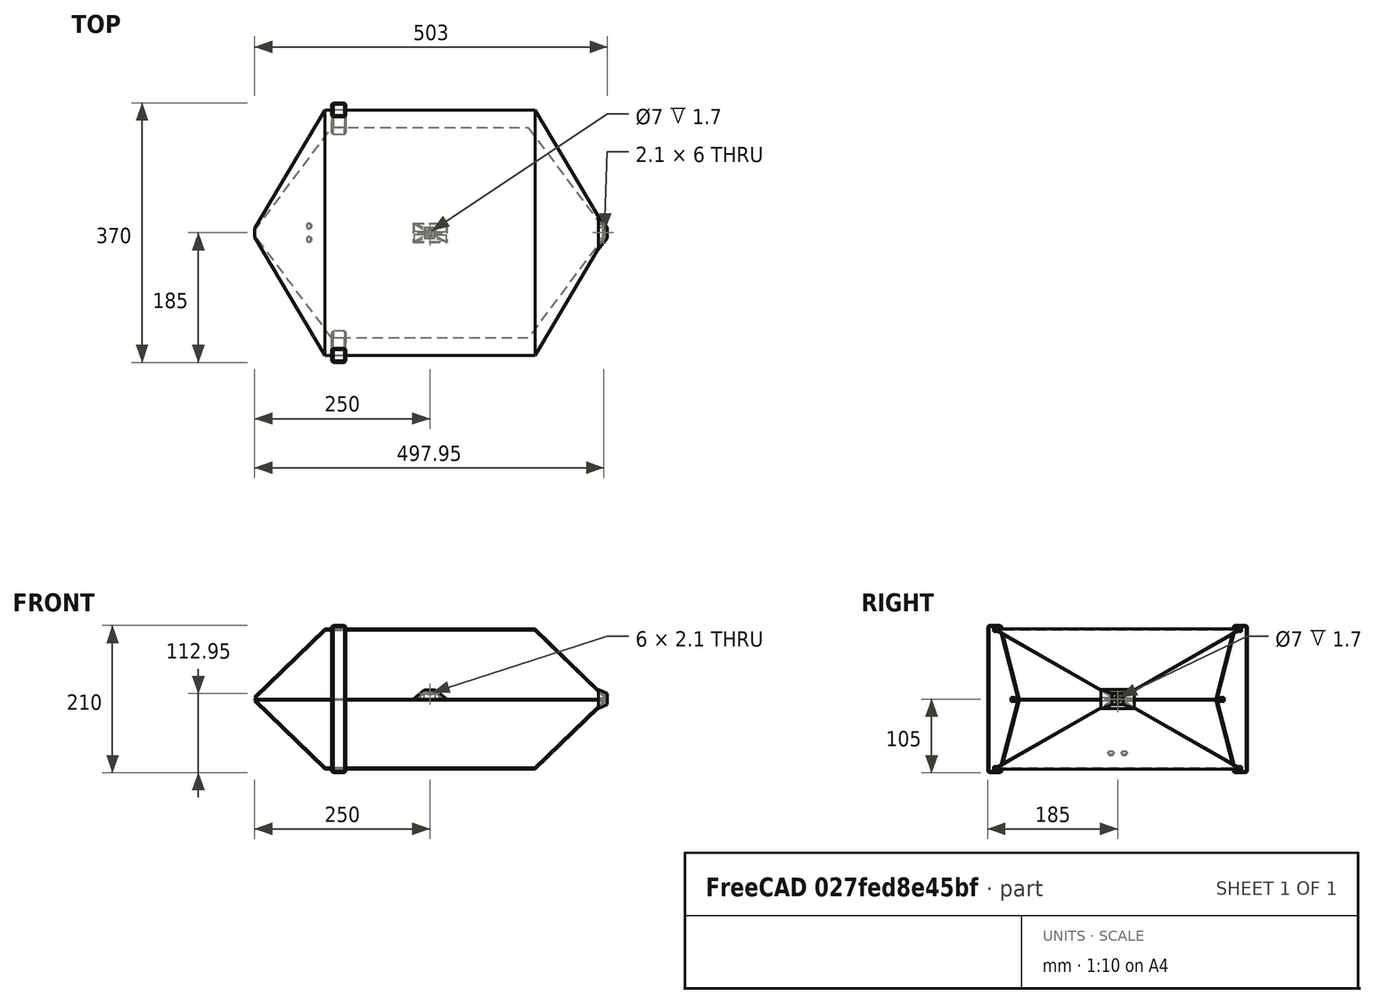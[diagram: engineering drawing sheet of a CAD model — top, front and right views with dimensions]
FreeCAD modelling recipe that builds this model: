
FCSTD DOCUMENT  (FreeCAD 0.21R33694 (Git))
Label: OpenTEMCell
License: All rights reserved
LicenseURL: http://en.wikipedia.org/wiki/All_rights_reserved
objects: TechDraw::DrawViewDimension×23, Sketcher::SketchObject×8, PartDesign::Pad×6, PartDesign::Body×5, PartDesign::AdditiveWedge×5, PartDesign::Mirrored×4, Part::Mirroring×4, App::Part×3, TechDraw::DrawViewPart×3, PartDesign::SubtractiveWedge×3, PartDesign::CoordinateSystem×2, TechDraw::DrawSVGTemplate×2, TechDraw::DrawViewBalloon×2, TechDraw::DrawPage×2, Spreadsheet::Sheet×1, PartDesign::Pocket×1, PartDesign::Chamfer×1, TechDraw::DrawViewSpreadsheet×1, TechDraw::DrawViewAnnotation×1, PartDesign::SubtractiveCylinder×1
note: 73 computed .brp shape members not serialized (recipe doc carries the construction recipe); baked Part::Feature solids carry a one-line shape summary decoded from their .brp

FEATURE [Spreadsheet::Sheet] Spreadsheet  label="Params"
  cells = A1='ShieldWidth; B1(ShieldWidth)==350 mm; D1='Width of the outer shield sections (affects FringeCapacitance); A2='SeptumWidth; B2(SeptumWidth)==300 mm; D2='Width of the middle septum layer (affects ApproxImpedance); A3='CenterSectionLength; B3(CenterSectionLength)==300 mm; D3='Length of the square center section of shields; A4='SeptumCenterSectionLength; B4(SeptumCenterSectionLength)==280 mm; D4='Length of the square center section of septum; A5='TaperSectionLength; B5(TaperSectionLength)==100 mm; D5='Tapered section horizontal length of shields; A7='UpperHeight; B7(UpperHeight)==100 mm; D7='Distance between septum and upper shield; A8='LowerHeight; B8(LowerHeight)==100 mm; D8='Distance between septum and lower shield; A10='ShieldTaperEndWidth; B10(ShieldTaperEndWidth)==12 mm; D10='For mounting the coaxial connectors; A11='ShieldTaperEndHeight; B11(ShieldTaperEndHeight)==6 mm; A12='SeptumTaperEndWidth; B12(SeptumTaperEndWidth)==6 mm; A13='MaterialThickness; B13(MaterialThickness)==1.6 mm; A15='Parameters below are calculated from inputs above; A17='SeptumTotalLength; B17(SeptumTotalLength)==CenterSectionLength + 2 * TaperSectionLength; D17='Total length for the middle septum layer; A18='UpperShieldTaperMaterialLength; B18(UpperShieldTaperMaterialLength)==sqrt((UpperHeight - ShieldTaperEndHeight / 2) ^ 2 + TaperSectionLength ^ 2); D18='Material length at the taper slope on each end of upper shield; A19='LowerShieldTaperMaterialLength; B19(LowerShieldTaperMaterialLength)==sqrt((LowerHeight - ShieldTaperEndHeight / 2) ^ 2 + TaperSectionLength ^ 2); A20='UpperShieldTotalLength; B20(UpperShieldTotalLength)==CenterSectionLength + UpperShieldTaperMaterialLength * 2; D20='Total material length for upper shield; A21='LowerShieldTotalLength; B21(LowerShieldTotalLength)==CenterSectionLength + LowerShieldTaperMaterialLength * 2; A23='FringeCapacitance; B23(FringeCapacitance)=0.03; C23='(empirical); A24='ApproxImpedance; B24==94 / (SeptumWidth / (UpperHeight + LowerHeight) + FringeCapacitance / 0.0885); C24='(ohm); D24='(valid only for UpperHeight = LowerHeight); A26='UpperTaperAngle; B26(UpperTaperAngle)==atan((UpperHeight - ShieldTaperEndHeight / 2) / TaperSectionLength); A27='LowerTaperAngle; B27(LowerTaperAngle)==atan((LowerHeight - ShieldTaperEndHeight / 2) / TaperSectionLength)
FEATURE [Sketcher::SketchObject] Sketch  label="SeptumSketch"
  FullyConstrained = true
  MapMode = 5
  Support = -> [XY_Plane001]
  expr: Constraints[14] = <<Params>>.SeptumTotalLength
  expr: Constraints[15] = <<Params>>.SeptumCenterSectionLength
  expr: Constraints[16] = <<Params>>.SeptumWidth
  expr: Constraints[17] = <<Params>>.SeptumTaperEndWidth
  sketch-geometry (8):
    g0: LineSegment StartX=-250 StartY=-3 StartZ=0 EndX=-250 EndY=3 EndZ=0
    g1: LineSegment StartX=-250 StartY=3 StartZ=0 EndX=-140 EndY=150 EndZ=0
    g2: LineSegment StartX=-140 StartY=150 StartZ=0 EndX=140 EndY=150 EndZ=0
    g3: LineSegment StartX=140 StartY=150 StartZ=0 EndX=250 EndY=3 EndZ=0
    g4: LineSegment StartX=250 StartY=3 StartZ=0 EndX=250 EndY=-3 EndZ=0
    g5: LineSegment StartX=250 StartY=-3 StartZ=0 EndX=140 EndY=-150 EndZ=0
    g6: LineSegment StartX=140 StartY=-150 StartZ=0 EndX=-140 EndY=-150 EndZ=0
    g7: LineSegment StartX=-140 StartY=-150 StartZ=0 EndX=-250 EndY=-3 EndZ=0
  constraints (18):
    c: Coincident(g0,g1)
    c: Coincident(g1,g2)
    c: Coincident(g3,g4)
    c: Coincident(g4,g5)
    c: Coincident(g5,g6)
    c: Coincident(g6,g7)
    c: Coincident(g7,g0)
    c: Symmetric(g6,g1,g-1)
    c: Symmetric(g5,g2,g-1)
    c: Symmetric(g2,g1,g-2)
    c: Coincident(g3,g2)
    c: Symmetric(g3,g4,g-1)
    c: Symmetric(g4,g0,g-2)
    c: Symmetric(g0,g3,g-2)
    c: DistanceX(g0,g4) = 500
    c: DistanceX(g2,g2) = 280
    c: DistanceY(g6,g1) = 300
    c: DistanceY(g0,g0) = 6
FEATURE [PartDesign::Pad] Pad  label="Septum001"
  Direction = (0,0,1)
  Length = 1.6
  Length2 = 10
  Profile = -> Sketch
  ReferenceAxis = -> Sketch [N_Axis]
  Reversed = true
  Type = 0
  expr: Length = <<Params>>.MaterialThickness
FEATURE [PartDesign::Body] Body  label="Septum"
  Group = -> [Sketch,Pad]
  Origin = -> Origin001
  Tip = -> Pad
FEATURE [Sketcher::SketchObject] Sketch001  label="UpperShieldCenterSectionSketch"
  FullyConstrained = true
  MapMode = 5
  Support = -> [XY_Plane]
  expr: Constraints[8] = <<Params>>.CenterSectionLength
  expr: Constraints[9] = <<Params>>.ShieldWidth
  sketch-geometry (4):
    g0: LineSegment StartX=-150 StartY=175 StartZ=0 EndX=150 EndY=175 EndZ=0
    g1: LineSegment StartX=150 StartY=175 StartZ=0 EndX=150 EndY=-175 EndZ=0
    g2: LineSegment StartX=150 StartY=-175 StartZ=0 EndX=-150 EndY=-175 EndZ=0
    g3: LineSegment StartX=-150 StartY=-175 StartZ=0 EndX=-150 EndY=175 EndZ=0
  constraints (11):
    c: Coincident(g0,g1)
    c: Coincident(g1,g2)
    c: Coincident(g2,g3)
    c: Coincident(g3,g0)
    c: Horizontal(g0)
    c: Horizontal(g2)
    c: Vertical(g1)
    c: Vertical(g3)
    c: DistanceX(g0,g0) = 300
    c: DistanceY(g3,g3) = 350
    c: Symmetric(g0,g2,g-1)
FEATURE [PartDesign::Pad] Pad001  label="UpperShieldCenterSection"
  Direction = (0,0,1)
  Length = 1.6
  Length2 = 10
  Profile = -> Sketch001
  ReferenceAxis = -> Sketch001 [N_Axis]
  Type = 0
  expr: Length = <<Params>>.MaterialThickness
FEATURE [PartDesign::CoordinateSystem] Local_CS  label="TaperCoordinateSystem"
  AttacherType = Attacher::AttachEngine3D
  AttachmentOffset = pos=(-150,0,0) rot=(0,1,0;0.770171rad)
  MapMode = 5
  Placement = pos=(-150,0,0) rot=(0,1,0;0.770171rad)
  Support = -> [XY_Plane]
  expr: .AttachmentOffset.Base.x = -<<Params>>.CenterSectionLength / 2
  expr: .AttachmentOffset.Rotation.Pitch = <<Params>>.UpperTaperAngle
  expr: .AttachmentOffset.Rotation.Roll = 0
FEATURE [Sketcher::SketchObject] Sketch002  label="UpperShieldTaperSectionSketch"
  FullyConstrained = true
  MapMode = 5
  Placement = pos=(-150,0,0) rot=(0,1,0;0.770171rad)
  Support = -> [Local_CS]
  expr: .AttachmentOffset.Rotation.Angle = 0
  expr: Constraints[6] = <<Params>>.ShieldTaperEndWidth
  expr: Constraints[7] = <<Params>>.ShieldWidth
  expr: Constraints[8] = <<Params>>.UpperShieldTaperMaterialLength
  sketch-geometry (4):
    g0: LineSegment StartX=1e-16 StartY=-175 StartZ=0 EndX=0 EndY=175 EndZ=0
    g1: LineSegment StartX=0 StartY=175 StartZ=0 EndX=-139.316 EndY=6 EndZ=0
    g2: LineSegment StartX=-139.316 StartY=6 StartZ=0 EndX=-139.316 EndY=-6 EndZ=0
    g3: LineSegment StartX=-139.316 StartY=-6 StartZ=0 EndX=0 EndY=-175 EndZ=0
  constraints (10):
    c: Coincident(g0,g1)
    c: Coincident(g1,g2)
    c: Coincident(g2,g3)
    c: Coincident(g3,g0)
    c: Symmetric(g0,g0,g-1)
    c: Symmetric(g1,g2,g-1)
    c: DistanceY(g2,g2) = 12
    c: DistanceY(g0,g0) = 350
    c: DistanceX(g1,g0) = 139.316
    c: PointOnObject(g0,g-2)
FEATURE [PartDesign::Pad] Pad002  label="UpperShieldTaperSection"
  BaseFeature = -> Pad001
  Direction = (0.696258,0,0.717792)
  Length = 1.6
  Length2 = 10
  Profile = -> Sketch002
  ReferenceAxis = -> Sketch002 [N_Axis]
  Type = 0
  expr: Length = <<Params>>.MaterialThickness
FEATURE [PartDesign::Mirrored] Mirrored  label="UpperTaperMirror"
  BaseFeature = -> Pad002
  MirrorPlane = -> YZ_Plane
  Originals = -> [Pad002]
FEATURE [PartDesign::Body] Body001  label="UpperShield"
  Group = -> [Sketch001,Pad001,Sketch002,Local_CS,Pad002,Mirrored]
  Origin = -> Origin
  Placement = pos=(0,0,100) rot=(1,0,0;3.14159rad)
  Tip = -> Mirrored
  expr: .Placement.Base.z = <<Params>>.UpperHeight
FEATURE [PartDesign::CoordinateSystem] Local_CS001  label="TaperCoordinateSystem001"
  AttacherType = Attacher::AttachEngine3D
  AttachmentOffset = pos=(-150,0,0) rot=(0,1,0;0.770171rad)
  MapMode = 5
  Placement = pos=(-150,0,0) rot=(0,1,0;0.770171rad)
  Support = -> [XY_Plane002]
  expr: .AttachmentOffset.Base.x = -<<Params>>.CenterSectionLength / 2
  expr: .AttachmentOffset.Rotation.Pitch = <<Params>>.LowerTaperAngle
  expr: .AttachmentOffset.Rotation.Roll = 0
FEATURE [Sketcher::SketchObject] Sketch003  label="LowerShieldCenterSectionSketch"
  FullyConstrained = true
  MapMode = 5
  Support = -> [XY_Plane002]
  expr: Constraints[8] = <<Params>>.CenterSectionLength
  expr: Constraints[9] = <<Params>>.ShieldWidth
  sketch-geometry (4):
    g0: LineSegment StartX=-150 StartY=175 StartZ=0 EndX=150 EndY=175 EndZ=0
    g1: LineSegment StartX=150 StartY=175 StartZ=0 EndX=150 EndY=-175 EndZ=0
    g2: LineSegment StartX=150 StartY=-175 StartZ=0 EndX=-150 EndY=-175 EndZ=0
    g3: LineSegment StartX=-150 StartY=-175 StartZ=0 EndX=-150 EndY=175 EndZ=0
  constraints (11):
    c: Coincident(g0,g1)
    c: Coincident(g1,g2)
    c: Coincident(g2,g3)
    c: Coincident(g3,g0)
    c: Horizontal(g0)
    c: Horizontal(g2)
    c: Vertical(g1)
    c: Vertical(g3)
    c: DistanceX(g0,g0) = 300
    c: DistanceY(g3,g3) = 350
    c: Symmetric(g0,g2,g-1)
FEATURE [PartDesign::Pad] Pad003  label="LowerShieldCenterSection"
  Direction = (0,0,1)
  Length = 1.6
  Length2 = 10
  Profile = -> Sketch003
  ReferenceAxis = -> Sketch003 [N_Axis]
  Type = 0
  expr: Length = <<Params>>.MaterialThickness
FEATURE [Sketcher::SketchObject] Sketch004  label="LowerShieldTaperSectionSketch"
  FullyConstrained = true
  MapMode = 5
  Placement = pos=(-150,0,0) rot=(0,1,0;0.770171rad)
  Support = -> [Local_CS001]
  expr: .AttachmentOffset.Rotation.Angle = 0
  expr: Constraints[6] = <<Params>>.ShieldTaperEndWidth
  expr: Constraints[7] = <<Params>>.ShieldWidth
  expr: Constraints[8] = <<Params>>.LowerShieldTaperMaterialLength
  sketch-geometry (4):
    g0: LineSegment StartX=0 StartY=-175 StartZ=0 EndX=0 EndY=175 EndZ=0
    g1: LineSegment StartX=0 StartY=175 StartZ=0 EndX=-139.316 EndY=6 EndZ=0
    g2: LineSegment StartX=-139.316 StartY=6 StartZ=0 EndX=-139.316 EndY=-6 EndZ=0
    g3: LineSegment StartX=-139.316 StartY=-6 StartZ=0 EndX=0 EndY=-175 EndZ=0
  constraints (10):
    c: Coincident(g0,g1)
    c: Coincident(g1,g2)
    c: Coincident(g2,g3)
    c: Coincident(g3,g0)
    c: Symmetric(g0,g0,g-1)
    c: Symmetric(g1,g2,g-1)
    c: DistanceY(g2,g2) = 12
    c: DistanceY(g0,g0) = 350
    c: DistanceX(g1,g0) = 139.316
    c: PointOnObject(g0,g-2)
FEATURE [PartDesign::Pad] Pad004  label="LowerShieldTaperSection"
  BaseFeature = -> Pad003
  Direction = (0.696258,0,0.717792)
  Length = 1.6
  Length2 = 10
  Profile = -> Sketch004
  ReferenceAxis = -> Sketch004 [N_Axis]
  Type = 0
  expr: Length = <<Params>>.MaterialThickness
FEATURE [PartDesign::Mirrored] Mirrored001  label="LowerTaperMirror"
  BaseFeature = -> Pad004
  MirrorPlane = -> YZ_Plane002
  Originals = -> [Pad004]
FEATURE [Sketcher::SketchObject] Sketch005  label="BindingPostHolesSketch"
  FullyConstrained = true
  MapMode = 5
  Placement = pos=(-150,0,0) rot=(0,1,0;0.770171rad)
  Support = -> [Local_CS001]
  sketch-geometry (2):
    g0: Circle CenterX=-32 CenterY=9.5 CenterZ=0 NormalX=0 NormalY=0 NormalZ=1 AngleXU=0 Radius=4
    g1: Circle CenterX=-32 CenterY=-9.5 CenterZ=0 NormalX=0 NormalY=0 NormalZ=1 AngleXU=0 Radius=4
  constraints (5):
    c: Symmetric(g0,g1,g-1)
    c: DistanceY(g1,g0) = 19
    c: Diameter(g0) = 8
    c: Equal(g1,g0)
    c: DistanceX(g1,g-1) = 32
FEATURE [PartDesign::Pocket] Pocket  label="BindingPostHoles"
  BaseFeature = -> Mirrored001
  Direction = (-0.696258,0,-0.717792)
  Length = 5
  Length2 = 5
  Profile = -> Sketch005
  ReferenceAxis = -> Sketch005 [N_Axis]
  Reversed = true
  Type = 1
FEATURE [PartDesign::Body] Body002  label="LowerShield"
  Group = -> [Sketch003,Pad003,Sketch004,Local_CS001,Pad004,Mirrored001,Sketch005,Pocket]
  Origin = -> Origin002
  Placement = pos=(0,0,-100) rot=(1,0,0;0rad)
  Tip = -> Pocket
  expr: .Placement.Base.z = -<<Params>>.LowerHeight
FEATURE [Sketcher::SketchObject] Sketch006  label="SideHolderSketch"
  FullyConstrained = true
  MapMode = 5
  Support = -> [XY_Plane003]
  expr: Constraints[31] = <<Params>>.LowerHeight
  expr: Constraints[38] = (<<Params>>.ShieldWidth - <<Params>>.SeptumWidth) / 2
  expr: Constraints[40] = <<Params>>.UpperHeight
  expr: Constraints[45] = <<Params>>.MaterialThickness + 5 mm
  expr: Constraints[46] = <<Params>>.MaterialThickness + 5 mm
  sketch-geometry (16):
    g0: LineSegment StartX=0 StartY=-105 StartZ=0 EndX=20 EndY=-105 EndZ=0
    g1: LineSegment StartX=20 StartY=-105 StartZ=0 EndX=20 EndY=-100 EndZ=0
    g2: LineSegment StartX=20 StartY=-100 StartZ=0 EndX=10 EndY=-100 EndZ=0
    g3: LineSegment StartX=10 StartY=-100 StartZ=0 EndX=10 EndY=-98.4 EndZ=0
    g4: LineSegment StartX=10 StartY=-98.4 StartZ=0 EndX=20 EndY=-98.4 EndZ=0
    g5: LineSegment StartX=20 StartY=-98.4 StartZ=0 EndX=45 EndY=-1.6 EndZ=0
    g6: LineSegment StartX=45 StartY=-1.6 StartZ=0 EndX=35 EndY=-1.6 EndZ=0
    g7: LineSegment StartX=35 StartY=-1.6 StartZ=0 EndX=35 EndY=0 EndZ=0
    g8: LineSegment StartX=35 StartY=0 StartZ=0 EndX=45 EndY=0 EndZ=0
    g9: LineSegment StartX=45 StartY=0 StartZ=0 EndX=20 EndY=98.4 EndZ=0
    g10: LineSegment StartX=20 StartY=98.4 StartZ=0 EndX=10 EndY=98.4 EndZ=0
    g11: LineSegment StartX=10 StartY=98.4 StartZ=0 EndX=10 EndY=100 EndZ=0
    g12: LineSegment StartX=10 StartY=100 StartZ=0 EndX=20 EndY=100 EndZ=0
    g13: LineSegment StartX=20 StartY=100 StartZ=0 EndX=20 EndY=105 EndZ=0
    g14: LineSegment StartX=20 StartY=105 StartZ=0 EndX=0 EndY=105 EndZ=0
    g15: LineSegment StartX=0 StartY=105 StartZ=0 EndX=0 EndY=-105 EndZ=0
  constraints (48):
    c: PointOnObject(g0,g-2)
    c: Horizontal(g0)
    c: Coincident(g0,g1)
    c: Vertical(g1)
    c: Coincident(g1,g2)
    c: Horizontal(g2)
    c: Coincident(g2,g3)
    c: Vertical(g3)
    c: Coincident(g3,g4)
    c: Horizontal(g4)
    c: Coincident(g4,g5)
    c: Coincident(g5,g6)
    c: Horizontal(g6)
    c: Coincident(g6,g7)
    c: Vertical(g7)
    c: Coincident(g7,g8)
    c: Horizontal(g8)
    c: Coincident(g8,g9)
    c: Coincident(g9,g10)
    c: Horizontal(g10)
    c: Coincident(g10,g11)
    c: Vertical(g11)
    c: Coincident(g11,g12)
    c: Horizontal(g12)
    c: Coincident(g12,g13)
    c: Vertical(g13)
    c: Coincident(g13,g14)
    c: PointOnObject(g14,g-2)
    c: Horizontal(g14)
    c: Coincident(g14,g15)
    c: Coincident(g15,g0)
    c: DistanceY(g2,g-1) = 100
    c: Vertical(g1,g4)
    c: Vertical(g9,g12)
    c: Vertical(g12,g1)
    c: Vertical(g8,g5)
    c: DistanceX(g0,g2) = 10
    c: Vertical(g3,g10)
    c: DistanceX(g3,g6) = 25
    c: DistanceX(g6,g6) = 10
    c: DistanceY(g-1,g11) = 100
    c: DistanceY(g13,g13) = 5
    c: DistanceY(g1,g1) = 5
    c: Equal(g4,g6)
    c: PointOnObject(g8,g-1)
    c: DistanceY(g10,g14) = 6.6
    c: DistanceY(g0,g3) = 6.6
    c: Equal(g3,g7)
FEATURE [PartDesign::Pad] Pad005  label="SideHolderBaseForm"
  Direction = (0,0,1)
  Length = 20
  Length2 = 10
  Profile = -> Sketch006
  ReferenceAxis = -> Sketch006 [N_Axis]
  Type = 0
FEATURE [PartDesign::Chamfer] Chamfer
  Angle = 45
  Base = -> Pad005 [Face18,Face17,Face16,Face15,Face1]
  BaseFeature = -> Pad005
  ChamferType = 0
  FlipDirection = false
  Size = 2
  Size2 = 1
  SupportTransform = false
  UseAllEdges = false
FEATURE [PartDesign::Body] Body003  label="SideHolder1"
  Group = -> [Sketch006,Pad005,Chamfer]
  Origin = -> Origin003
  Placement = pos=(120,-185,0) rot=(0.57735,0.57735,0.57735;2.0944rad)
  Tip = -> Chamfer
  expr: .Placement.Base.x = <<Params>>.SeptumCenterSectionLength / 2 - 20 mm
  expr: .Placement.Base.y = -<<Params>>.ShieldWidth / 2 - 10 mm
FEATURE [Part::Mirroring] mirror  label="SideHolder2 (mirror)"
  Base = (0,0,0)
  Normal = (1,0,0)
  Source = -> Body003
FEATURE [Part::Mirroring] mirror002  label="SideHolder4 (mirror)"
  Base = (0,0,0)
  Normal = (0,1,0)
  Source = -> Body003
FEATURE [Part::Mirroring] mirror003  label="SideHolder3 (mirror)"
  Base = (0,0,0)
  Normal = (1,0,0)
  Source = -> mirror002
FEATURE [App::Part] Part  label="SideHolders"
  Group = -> [Body003,mirror002,mirror003,mirror]
  Origin = -> Origin004
FEATURE [TechDraw::DrawSVGTemplate] Template
  Height = 297
  Orientation = 0
  Width = 210
FEATURE [TechDraw::DrawViewSpreadsheet] Sheet
  CellEnd = D27
  CellStart = A1
  Font = osifont
  LineWidth = 0.35
  LockPosition = false
  Rotation = 0
  Scale = 0.5
  ScaleType = 2
  Source = -> Spreadsheet
  Symbol = <blob: 18333 chars omitted>
  TextSize = 16
  X = 105.113
  Y = 218.016
FEATURE [TechDraw::DrawViewAnnotation] Annotation  label="Title"
  Font = osifont
  LineSpace = 80
  LockPosition = false
  MaxWidth = -1
  Rotation = 0
  Scale = 0.2
  ScaleType = 0
  Text = Open TEM cell design parameters | (generated from OpenTEMCell.FCStd)
  TextSize = 5
  TextStyle = 0
  X = 100.663
  Y = 282.927
FEATURE [TechDraw::DrawSVGTemplate] Template001
  Height = 420
  Orientation = 1
  Template = <path>
  Width = 594
FEATURE [Sketcher::SketchObject] Sketch007  label="ShieldMaterialSketch"
  FullyConstrained = true
  expr: Constraints[14] = <<Params>>.ShieldWidth
  expr: Constraints[15] = <<Params>>.CenterSectionLength
  expr: Constraints[16] = <<Params>>.UpperShieldTaperMaterialLength
  expr: Constraints[17] = <<Params>>.ShieldTaperEndWidth
  sketch-geometry (12):
    g0: LineSegment StartX=-289.316 StartY=-6 StartZ=0 EndX=-289.316 EndY=6 EndZ=0
    g1: LineSegment StartX=-289.316 StartY=6 StartZ=0 EndX=-150 EndY=175 EndZ=0
    g2: LineSegment StartX=-150 StartY=175 StartZ=0 EndX=150 EndY=175 EndZ=0
    g3: LineSegment StartX=150 StartY=175 StartZ=0 EndX=289.316 EndY=6 EndZ=0
    g4: LineSegment StartX=289.316 StartY=6 StartZ=0 EndX=289.316 EndY=-6 EndZ=0
    g5: LineSegment StartX=289.316 StartY=-6 StartZ=0 EndX=150 EndY=-175 EndZ=0
    g6: LineSegment StartX=150 StartY=-175 StartZ=0 EndX=-150 EndY=-175 EndZ=0
    g7: LineSegment StartX=-150 StartY=-175 StartZ=0 EndX=-289.316 EndY=-6 EndZ=0
    g8: LineSegment StartX=-150 StartY=175 StartZ=0 EndX=-150 EndY=-175 EndZ=0
    g9: LineSegment StartX=150 StartY=175 StartZ=0 EndX=150 EndY=-175 EndZ=0
    g10: Circle CenterX=-182 CenterY=9.5 CenterZ=0 NormalX=0 NormalY=0 NormalZ=1 AngleXU=0 Radius=4
    g11: Circle CenterX=-182 CenterY=-9.5 CenterZ=0 NormalX=0 NormalY=0 NormalZ=1 AngleXU=0 Radius=4
  constraints (27):
    c: Coincident(g0,g1)
    c: Coincident(g1,g2)
    c: Coincident(g2,g3)
    c: Coincident(g3,g4)
    c: Coincident(g4,g5)
    c: Coincident(g5,g6)
    c: Coincident(g6,g7)
    c: Coincident(g7,g0)
    c: Symmetric(g0,g0,g-1)
    c: Symmetric(g3,g4,g-1)
    c: Symmetric(g4,g0,g-2)
    c: Symmetric(g1,g2,g-2)
    c: Symmetric(g6,g5,g-2)
    c: Symmetric(g5,g2,g-1)
    c: DistanceY(g5,g2) = 350
    c: DistanceX(g2,g2) = 300
    c: DistanceX(g0,g1) = 139.316
    c: DistanceY(g0,g0) = 12
    c: Coincident(g8,g1)
    c: Coincident(g8,g6)
    c: Coincident(g9,g2)
    c: Coincident(g9,g5)
    c: Symmetric(g11,g10,g-1)
    c: Equal(g11,g10)
    c: Diameter(g10) = 8
    c: DistanceY(g11,g10) = 19
    c: DistanceX(g10,g1) = 32
FEATURE [App::Part] Part001  label="TEMCell"
  Group = -> [Body,Body001,Body002,Sketch007]
  Origin = -> Origin005
FEATURE [TechDraw::DrawViewPart] View  label="SideView"
  CoarseView = true
  Direction = (0,-1,0)
  Focus = 100
  HardHidden = false
  IsoCount = 0
  IsoHidden = false
  IsoVisible = false
  LockPosition = true
  Perspective = false
  Rotation = 0
  Scale = 0.2
  ScaleType = 0
  ScrubCount = 0
  SeamHidden = false
  SeamVisible = true
  SmoothHidden = false
  SmoothVisible = true
  Source = -> [Part001]
  X = 100
  XDirection = (1,0,0)
  Y = 50
FEATURE [TechDraw::DrawViewPart] View001  label="TopView"
  CoarseView = true
  Direction = (0,0,1)
  Focus = 100
  HardHidden = true
  IsoCount = 0
  IsoHidden = false
  IsoVisible = false
  LockPosition = true
  Perspective = false
  Rotation = 0
  Scale = 0.2
  ScaleType = 0
  ScrubCount = 0
  SeamHidden = false
  SeamVisible = true
  SmoothHidden = false
  SmoothVisible = true
  Source = -> [Part001]
  X = 100
  XDirection = (1,0,0)
  Y = 120
FEATURE [TechDraw::DrawViewDimension] Dimension
  AngleOverride = false
  Arbitrary = false
  ArbitraryTolerances = false
  EqualTolerance = true
  ExtensionAngle = 0
  FormatSpec = %.2w
  FormatSpecOverTolerance = %+.2w
  FormatSpecUnderTolerance = %+.2w
  Inverted = false
  LineAngle = 0
  LockPosition = false
  MeasureType = 1
  OverTolerance = 0
  References2D = -> [View001]
  Rotation = 0
  Scale = 0.2
  ScaleType = 0
  TheoreticalExact = false
  Type = 2
  UnderTolerance = 0
  X = 65.3734
  Y = 0.232473
FEATURE [TechDraw::DrawViewDimension] Dimension001
  AngleOverride = false
  Arbitrary = false
  ArbitraryTolerances = false
  EqualTolerance = true
  ExtensionAngle = 0
  FormatSpec = %.2w
  FormatSpecOverTolerance = %+.2w
  FormatSpecUnderTolerance = %+.2w
  Inverted = false
  LineAngle = 0
  LockPosition = false
  MeasureType = 1
  OverTolerance = 0
  References2D = -> [View001]
  Rotation = 0
  Scale = 0.2
  ScaleType = 0
  TheoreticalExact = false
  Type = 1
  UnderTolerance = 0
  X = -2.63812
  Y = -90.4559
FEATURE [TechDraw::DrawViewDimension] Dimension002
  AngleOverride = false
  Arbitrary = false
  ArbitraryTolerances = false
  EqualTolerance = true
  ExtensionAngle = 0
  FormatSpec = %.2w
  FormatSpecOverTolerance = %+.2w
  FormatSpecUnderTolerance = %+.2w
  Inverted = false
  LineAngle = 0
  LockPosition = false
  MeasureType = 1
  OverTolerance = 0
  References2D = -> [View001]
  Rotation = 0
  Scale = 0.2
  ScaleType = 0
  TheoreticalExact = false
  Type = 2
  UnderTolerance = 0
  X = -68.9831
  Y = -1.17301
FEATURE [TechDraw::DrawViewDimension] Dimension003
  AngleOverride = false
  Arbitrary = false
  ArbitraryTolerances = false
  EqualTolerance = true
  ExtensionAngle = 0
  FormatSpec = %.2w
  FormatSpecOverTolerance = %+.2w
  FormatSpecUnderTolerance = %+.2w
  Inverted = false
  LineAngle = 0
  LockPosition = false
  MeasureType = 1
  OverTolerance = 0
  References2D = -> [View001]
  Rotation = 0
  Scale = 0.2
  ScaleType = 0
  TheoreticalExact = false
  Type = 1
  UnderTolerance = 0
  X = -2.84272
  Y = -38.2038
FEATURE [TechDraw::DrawViewDimension] Dimension004
  AngleOverride = false
  Arbitrary = false
  ArbitraryTolerances = false
  EqualTolerance = true
  ExtensionAngle = 0
  FormatSpec = %.2w
  FormatSpecOverTolerance = %+.2w
  FormatSpecUnderTolerance = %+.2w
  Inverted = false
  LineAngle = 0
  LockPosition = false
  MeasureType = 1
  OverTolerance = 0
  References2D = -> [View001]
  Rotation = 0
  Scale = 0.2
  ScaleType = 0
  TheoreticalExact = false
  Type = 1
  UnderTolerance = 0
  X = 41.4458
  Y = -90.4401
FEATURE [TechDraw::DrawViewDimension] Dimension005
  AngleOverride = false
  Arbitrary = false
  ArbitraryTolerances = false
  EqualTolerance = true
  ExtensionAngle = 0
  FormatSpec = %.2w
  FormatSpecOverTolerance = %+.2w
  FormatSpecUnderTolerance = %+.2w
  Inverted = false
  LineAngle = 0
  LockPosition = false
  MeasureType = 1
  OverTolerance = 0
  References2D = -> [View001]
  Rotation = 0
  Scale = 0.2
  ScaleType = 0
  TheoreticalExact = false
  Type = 1
  UnderTolerance = 0
  X = -40.6547
  Y = -90.4134
FEATURE [TechDraw::DrawViewDimension] Dimension006
  AngleOverride = false
  Arbitrary = false
  ArbitraryTolerances = false
  EqualTolerance = true
  ExtensionAngle = 0
  FormatSpec = %.2w
  FormatSpecOverTolerance = %+.2w
  FormatSpecUnderTolerance = %+.2w
  Inverted = false
  LineAngle = 0
  LockPosition = false
  MeasureType = 1
  OverTolerance = 0
  References2D = -> [View]
  Rotation = 0
  Scale = 0.2
  ScaleType = 0
  TheoreticalExact = false
  Type = 2
  UnderTolerance = 0
  X = 68.4123
  Y = -9.20589
FEATURE [TechDraw::DrawViewDimension] Dimension007
  AngleOverride = false
  Arbitrary = false
  ArbitraryTolerances = false
  EqualTolerance = true
  ExtensionAngle = 0
  FormatSpec = %.2w
  FormatSpecOverTolerance = %+.2w
  FormatSpecUnderTolerance = %+.2w
  Inverted = false
  LineAngle = 0
  LockPosition = false
  MeasureType = 1
  OverTolerance = 0
  References2D = -> [View]
  Rotation = 0
  Scale = 0.2
  ScaleType = 0
  TheoreticalExact = false
  Type = 2
  UnderTolerance = 0
  X = 68.4483
  Y = 11.6305
FEATURE [TechDraw::DrawViewBalloon] Balloon
  BubbleShape = 1
  EndType = 0
  EndTypeScale = 1
  KinkLength = 5
  LockPosition = false
  OriginX = -195
  OriginY = -2.84e-14
  Rotation = 0
  Scale = 0.2
  ScaleType = 0
  ShapeScale = 1
  SourceView = -> View
  Text = Septum copper on centerline
  TextWrapLen = -1
  X = -24.6991
  Y = 17.3265
FEATURE [TechDraw::DrawViewBalloon] Balloon001
  BubbleShape = 1
  EndType = 0
  EndTypeScale = 1
  KinkLength = 5
  LockPosition = false
  OriginX = -200
  OriginY = 51.5
  Rotation = 0
  Scale = 0.2
  ScaleType = 0
  ShapeScale = 1
  SourceView = -> View
  Text = Shield copper on outside
  TextWrapLen = -1
  X = -341.033
  Y = 61.1795
FEATURE [TechDraw::DrawViewDimension] Dimension008
  AngleOverride = false
  Arbitrary = false
  ArbitraryTolerances = false
  EqualTolerance = true
  ExtensionAngle = 0
  FormatSpec = %.2w
  FormatSpecOverTolerance = %+.2w
  FormatSpecUnderTolerance = %+.2w
  Inverted = false
  LineAngle = 0
  LockPosition = false
  MeasureType = 1
  OverTolerance = 0
  References2D = -> [View]
  Rotation = 0
  Scale = 0.2
  ScaleType = 0
  TheoreticalExact = false
  Type = 0
  UnderTolerance = 0
  X = 44.665
  Y = 15.397
FEATURE [TechDraw::DrawViewDimension] Dimension009
  AngleOverride = false
  Arbitrary = false
  ArbitraryTolerances = false
  EqualTolerance = true
  ExtensionAngle = 0
  FormatSpec = %.2w
  FormatSpecOverTolerance = %+.2w
  FormatSpecUnderTolerance = %+.2w
  Inverted = false
  LineAngle = 0
  LockPosition = false
  MeasureType = 1
  OverTolerance = 0
  References2D = -> [View001]
  Rotation = 0
  Scale = 0.2
  ScaleType = 0
  TheoreticalExact = false
  Type = 1
  UnderTolerance = 0
  X = -36.8575
  Y = -38.192
FEATURE [TechDraw::DrawViewDimension] Dimension010
  AngleOverride = false
  Arbitrary = false
  ArbitraryTolerances = false
  EqualTolerance = true
  ExtensionAngle = 0
  FormatSpec = %.2w
  FormatSpecOverTolerance = %+.2w
  FormatSpecUnderTolerance = %+.2w
  Inverted = false
  LineAngle = 0
  LockPosition = false
  MeasureType = 1
  OverTolerance = 0
  References2D = -> [View001]
  Rotation = 0
  Scale = 0.2
  ScaleType = 0
  TheoreticalExact = false
  Type = 1
  UnderTolerance = 0
  X = 41.1425
  Y = -38.192
FEATURE [TechDraw::DrawViewDimension] Dimension011
  AngleOverride = false
  Arbitrary = false
  ArbitraryTolerances = false
  EqualTolerance = true
  ExtensionAngle = 0
  FormatSpec = %.2w
  FormatSpecOverTolerance = %+.2w
  FormatSpecUnderTolerance = %+.2w
  Inverted = false
  LineAngle = 0
  LockPosition = false
  MeasureType = 1
  OverTolerance = 0
  References2D = -> [View001]
  Rotation = 0
  Scale = 0.2
  ScaleType = 0
  TheoreticalExact = false
  Type = 2
  UnderTolerance = 0
  X = 55.3244
  Y = -3.6823
FEATURE [TechDraw::DrawPage] Page  label="DimensionDrawing"
  KeepUpdated = true
  NextBalloonIndex = 5
  ProjectionType = 0
  Scale = 0.2
  Template = -> Template
  Views = -> [View,View001,Sheet,Annotation,Dimension,Dimension001,Dimension002,Dimension003,Dimension004,Dimension005,Dimension006,Dimension007,Balloon,Balloon001,Dimension008,Dimension009,Dimension010,Dimension011]
FEATURE [TechDraw::DrawViewPart] View004  label="SketchView"
  CoarseView = false
  Direction = (0,0,1)
  Focus = 100
  HardHidden = false
  IsoCount = 0
  IsoHidden = false
  IsoVisible = false
  LockPosition = false
  Perspective = false
  Rotation = 0
  ScaleType = 0
  ScrubCount = 0
  SeamHidden = false
  SeamVisible = true
  SmoothHidden = false
  SmoothVisible = true
  Source = -> [Sketch,Sketch007]
  X = 297
  XDirection = (1,0,0)
  Y = 210
FEATURE [TechDraw::DrawViewDimension] Dimension012
  AngleOverride = false
  Arbitrary = false
  ArbitraryTolerances = false
  EqualTolerance = true
  ExtensionAngle = 0
  FormatSpec = %.2w
  FormatSpecOverTolerance = %+.2w
  FormatSpecUnderTolerance = %+.2w
  Inverted = false
  LineAngle = 0
  LockPosition = false
  MeasureType = 1
  OverTolerance = 0
  References2D = -> [View004]
  Rotation = 0
  ScaleType = 0
  TheoreticalExact = false
  Type = 1
  UnderTolerance = 0
  X = -0.606495
  Y = 190.753
FEATURE [TechDraw::DrawViewDimension] Dimension013
  AngleOverride = false
  Arbitrary = false
  ArbitraryTolerances = false
  EqualTolerance = true
  ExtensionAngle = 0
  FormatSpec = %.2w
  FormatSpecOverTolerance = %+.2w
  FormatSpecUnderTolerance = %+.2w
  Inverted = false
  LineAngle = 0
  LockPosition = false
  MeasureType = 1
  OverTolerance = 0
  References2D = -> [View004]
  Rotation = 0
  ScaleType = 0
  TheoreticalExact = false
  Type = 1
  UnderTolerance = 0
  X = 0.68551
  Y = 159.726
FEATURE [TechDraw::DrawViewDimension] Dimension014
  AngleOverride = false
  Arbitrary = false
  ArbitraryTolerances = false
  EqualTolerance = true
  ExtensionAngle = 0
  FormatSpec = %.2w
  FormatSpecOverTolerance = %+.2w
  FormatSpecUnderTolerance = %+.2w
  Inverted = false
  LineAngle = 0
  LockPosition = false
  MeasureType = 1
  OverTolerance = 0
  References2D = -> [View004]
  Rotation = 0
  ScaleType = 0
  TheoreticalExact = false
  Type = 2
  UnderTolerance = 0
  X = 256.973
  Y = -9.65739
FEATURE [TechDraw::DrawViewDimension] Dimension015
  AngleOverride = false
  Arbitrary = false
  ArbitraryTolerances = false
  EqualTolerance = true
  ExtensionAngle = 0
  FormatSpec = %.2w
  FormatSpecOverTolerance = %+.2w
  FormatSpecUnderTolerance = %+.2w
  Inverted = false
  LineAngle = 0
  LockPosition = false
  MeasureType = 1
  OverTolerance = 0
  References2D = -> [View004]
  Rotation = 0
  ScaleType = 0
  TheoreticalExact = false
  Type = 2
  UnderTolerance = 0
  X = 282.6
  Y = -28.9292
FEATURE [TechDraw::DrawViewDimension] Dimension016
  AngleOverride = false
  Arbitrary = false
  ArbitraryTolerances = false
  EqualTolerance = true
  ExtensionAngle = 0
  FormatSpec = %.2w
  FormatSpecOverTolerance = %+.2w
  FormatSpecUnderTolerance = %+.2w
  Inverted = false
  LineAngle = 0
  LockPosition = false
  MeasureType = 1
  OverTolerance = 0
  References2D = -> [View004]
  Rotation = 0
  ScaleType = 0
  TheoreticalExact = false
  Type = 1
  UnderTolerance = 0
  X = 235
  Y = 190.557
FEATURE [TechDraw::DrawViewDimension] Dimension017
  AngleOverride = false
  Arbitrary = false
  ArbitraryTolerances = false
  EqualTolerance = true
  ExtensionAngle = 0
  FormatSpec = %.2w
  FormatSpecOverTolerance = %+.2w
  FormatSpecUnderTolerance = %+.2w
  Inverted = false
  LineAngle = 0
  LockPosition = false
  MeasureType = 1
  OverTolerance = 0
  References2D = -> [View004]
  Rotation = 0
  ScaleType = 0
  TheoreticalExact = false
  Type = 1
  UnderTolerance = 0
  X = -203.852
  Y = 191.022
FEATURE [TechDraw::DrawViewDimension] Dimension018
  AngleOverride = false
  Arbitrary = false
  ArbitraryTolerances = false
  EqualTolerance = true
  ExtensionAngle = 0
  FormatSpec = %.2w
  FormatSpecOverTolerance = %+.2w
  FormatSpecUnderTolerance = %+.2w
  Inverted = false
  LineAngle = 0
  LockPosition = false
  MeasureType = 1
  OverTolerance = 0
  References2D = -> [View004]
  Rotation = 0
  ScaleType = 0
  TheoreticalExact = false
  Type = 1
  UnderTolerance = 0
  X = -197.324
  Y = 159.821
FEATURE [TechDraw::DrawViewDimension] Dimension019
  AngleOverride = false
  Arbitrary = false
  ArbitraryTolerances = false
  EqualTolerance = true
  ExtensionAngle = 0
  FormatSpec = %.2w
  FormatSpecOverTolerance = %+.2w
  FormatSpecUnderTolerance = %+.2w
  Inverted = false
  LineAngle = 0
  LockPosition = false
  MeasureType = 1
  OverTolerance = 0
  References2D = -> [View004]
  Rotation = 0
  ScaleType = 0
  TheoreticalExact = false
  Type = 2
  UnderTolerance = 0
  X = -140
  Y = 1.5
FEATURE [TechDraw::DrawViewDimension] Dimension020
  AngleOverride = false
  Arbitrary = false
  ArbitraryTolerances = false
  EqualTolerance = true
  ExtensionAngle = 0
  FormatSpec = %.2w
  FormatSpecOverTolerance = %+.2w
  FormatSpecUnderTolerance = %+.2w
  Inverted = false
  LineAngle = 0
  LockPosition = false
  MeasureType = 1
  OverTolerance = 0
  References2D = -> [View004]
  Rotation = 0
  ScaleType = 0
  TheoreticalExact = false
  Type = 2
  UnderTolerance = 0
  X = -150
  Y = 1.5
FEATURE [TechDraw::DrawViewDimension] Dimension021
  AngleOverride = false
  Arbitrary = false
  ArbitraryTolerances = false
  EqualTolerance = true
  ExtensionAngle = 0
  FormatSpec = %.2w
  FormatSpecOverTolerance = %+.2w
  FormatSpecUnderTolerance = %+.2w
  Inverted = false
  LineAngle = 0
  LockPosition = false
  MeasureType = 1
  OverTolerance = 0
  References2D = -> [View004]
  Rotation = 0
  ScaleType = 0
  TheoreticalExact = false
  Type = 1
  UnderTolerance = 0
  X = 0.897523
  Y = -189.506
FEATURE [TechDraw::DrawViewDimension] Dimension022
  AngleOverride = false
  Arbitrary = false
  ArbitraryTolerances = false
  EqualTolerance = true
  ExtensionAngle = 0
  FormatSpec = %.2w
  FormatSpecOverTolerance = %+.2w
  FormatSpecUnderTolerance = %+.2w
  Inverted = false
  LineAngle = 0
  LockPosition = false
  MeasureType = 1
  OverTolerance = 0
  References2D = -> [View004]
  Rotation = 0
  ScaleType = 0
  TheoreticalExact = false
  Type = 1
  UnderTolerance = 0
  X = 0.448761
  Y = -182.8
FEATURE [TechDraw::DrawPage] Page001  label="CutTemplate"
  KeepUpdated = true
  NextBalloonIndex = 1
  ProjectionType = 0
  Template = -> Template001
  Views = -> [View004,Dimension012,Dimension013,Dimension014,Dimension015,Dimension016,Dimension017,Dimension018,Dimension019,Dimension020,Dimension021,Dimension022]
FEATURE [PartDesign::AdditiveWedge] Wedge  label="OutsideCone"
  AttacherType = Attacher::AttachEngine3D
  MapMode = 3
  Placement = pos=(0,0,0) rot=(1,0,0;1.5708rad)
  Support = -> [XY_Plane007]
  X2max = 8
  X2min = -8
  Xmax = 23.9
  Xmin = -23.9
  Ymax = 13
  Ymin = 0
  Z2max = 8
  Z2min = -8
  Zmax = 13.7
  Zmin = -13.7
  expr: Xmax = <<Params>>.ShieldTaperEndWidth / 2 + 10 mm * (<<Params>>.ShieldWidth - <<Params>>.ShieldTaperEndWidth) / <<Params>>.TaperSectionLength / 2 + 1 mm
  expr: Xmin = -(<<Params>>.ShieldTaperEndWidth / 2 + 10 mm * (<<Params>>.ShieldWidth - <<Params>>.ShieldTaperEndWidth) / <<Params>>.TaperSectionLength / 2) - 1 mm
  expr: Zmax = <<Params>>.ShieldTaperEndHeight / 2 + 10 mm * (<<Params>>.LowerHeight - <<Params>>.ShieldTaperEndHeight / 2) / <<Params>>.TaperSectionLength + 1 mm
  expr: Zmin = -(<<Params>>.ShieldTaperEndHeight / 2 + 10 mm * (<<Params>>.LowerHeight - <<Params>>.ShieldTaperEndHeight / 2) / <<Params>>.TaperSectionLength) - 1 mm
FEATURE [PartDesign::SubtractiveWedge] Wedge001  label="InsideCone"
  AttacherType = Attacher::AttachEngine3D
  BaseFeature = -> Wedge
  MapMode = 3
  Placement = pos=(0,0,0) rot=(1,0,0;1.5708rad)
  Support = -> [XY_Plane007]
  X2max = 6
  X2min = -6
  Xmax = 22.9
  Xmin = -22.9
  Ymax = 10
  Ymin = 0
  Z2max = 3
  Z2min = -3
  Zmax = 12.7
  Zmin = -12.7
  expr: X2max = <<Params>>.ShieldTaperEndWidth / 2
  expr: X2min = -<<Params>>.ShieldTaperEndWidth / 2
  expr: Xmax = <<Params>>.ShieldTaperEndWidth / 2 + 10 mm * (<<Params>>.ShieldWidth - <<Params>>.ShieldTaperEndWidth) / <<Params>>.TaperSectionLength / 2
  expr: Xmin = -(<<Params>>.ShieldTaperEndWidth / 2 + 10 mm * (<<Params>>.ShieldWidth - <<Params>>.ShieldTaperEndWidth) / <<Params>>.TaperSectionLength / 2)
  expr: Z2max = <<Params>>.ShieldTaperEndHeight / 2
  expr: Z2min = -<<Params>>.ShieldTaperEndHeight / 2
  expr: Zmax = <<Params>>.ShieldTaperEndHeight / 2 + 10 mm * (<<Params>>.UpperHeight - <<Params>>.ShieldTaperEndHeight / 2) / <<Params>>.TaperSectionLength
  expr: Zmin = -(<<Params>>.ShieldTaperEndHeight / 2 + 10 mm * (<<Params>>.LowerHeight - <<Params>>.ShieldTaperEndHeight / 2) / <<Params>>.TaperSectionLength)
FEATURE [PartDesign::SubtractiveWedge] Wedge002  label="SMArectangle"
  AttacherType = Attacher::AttachEngine3D
  BaseFeature = -> Wedge001
  MapMode = 3
  Placement = pos=(0,0,0) rot=(1,0,0;1.5708rad)
  Support = -> [XY_Plane007]
  X2max = 6.5
  X2min = -6.5
  Xmax = 6.5
  Xmin = -6.5
  Ymax = 11
  Ymin = 0
  Z2max = 6.5
  Z2min = -6.5
  Zmax = 6.5
  Zmin = -6.5
FEATURE [PartDesign::SubtractiveCylinder] Cylinder  label="SMAhole"
  Angle = 360
  AttacherType = Attacher::AttachEngine3D
  BaseFeature = -> Wedge002
  FirstAngle = 0
  Height = 25
  MapMode = 5
  Radius = 3.5
  SecondAngle = 0
  Support = -> [XY_Plane007]
FEATURE [PartDesign::AdditiveWedge] Wedge004  label="MidHolderTop"
  AttacherType = Attacher::AttachEngine3D
  BaseFeature = -> Cylinder
  MapMode = 3
  Placement = pos=(0,0,0) rot=(1,0,0;1.5708rad)
  Support = -> [XY_Plane007]
  X2max = 9
  X2min = 8
  Xmax = 22.9
  Xmin = 8
  Ymax = 10
  Ymin = 0
  Z2max = 0
  Z2min = -1.5
  Zmax = 0
  Zmin = -1.5
  expr: Xmax = <<Params>>.ShieldTaperEndWidth / 2 + 10 mm * (<<Params>>.ShieldWidth - <<Params>>.ShieldTaperEndWidth) / <<Params>>.TaperSectionLength / 2
FEATURE [PartDesign::AdditiveWedge] Wedge005  label="MidHolderBottom"
  AttacherType = Attacher::AttachEngine3D
  BaseFeature = -> Wedge004
  MapMode = 3
  Placement = pos=(0,0,0) rot=(1,0,0;1.5708rad)
  Support = -> [XY_Plane007]
  X2max = 11
  X2min = 8
  Xmax = 22.9
  Xmin = 8
  Ymax = 10
  Ymin = 0
  Z2max = 3.1
  Z2min = 1.6
  Zmax = 3.1
  Zmin = 1.6
  expr: Xmax = <<Params>>.ShieldTaperEndWidth / 2 + 10 mm * (<<Params>>.ShieldWidth - <<Params>>.ShieldTaperEndWidth) / <<Params>>.TaperSectionLength / 2
  expr: Z2max = <<Params>>.MaterialThickness + 1.5 mm
  expr: Z2min = <<Params>>.MaterialThickness
  expr: Zmax = <<Params>>.MaterialThickness + 1.5 mm
  expr: Zmin = <<Params>>.MaterialThickness
FEATURE [PartDesign::AdditiveWedge] Wedge006  label="MidHolderSide"
  AttacherType = Attacher::AttachEngine3D
  BaseFeature = -> Wedge005
  MapMode = 3
  Placement = pos=(0,0,0) rot=(1,0,0;1.5708rad)
  Support = -> [XY_Plane007]
  X2max = 12
  X2min = 8.1
  Xmax = 22.9
  Xmin = 16.3636
  Ymax = 9
  Ymin = 0
  Z2max = 1.6
  Z2min = 0
  Zmax = 1.6
  Zmin = 0
  expr: Xmax = <<Params>>.ShieldTaperEndWidth / 2 + 10 mm * (<<Params>>.ShieldWidth - <<Params>>.ShieldTaperEndWidth) / <<Params>>.TaperSectionLength / 2
  expr: Xmin = <<Params>>.SeptumTaperEndWidth / 2 + 10 mm * (<<Params>>.SeptumWidth - <<Params>>.SeptumTaperEndWidth) / (<<Params>>.SeptumTotalLength - <<Params>>.SeptumCenterSectionLength)
  expr: Z2max = <<Params>>.MaterialThickness
  expr: Z2min = 0
  expr: Zmax = <<Params>>.MaterialThickness
  expr: Zmin = 0
FEATURE [PartDesign::Mirrored] Mirrored003  label="MidHolderMirror"
  BaseFeature = -> Wedge006
  MirrorPlane = -> YZ_Plane007
  Originals = -> [Wedge004,Wedge005,Wedge006]
  Placement = pos=(0,0,0) rot=(1,0,0;1.5708rad)
  Refine = true
FEATURE [PartDesign::SubtractiveWedge] Wedge007  label="SMAhole_printsupport"
  AttacherType = Attacher::AttachEngine3D
  BaseFeature = -> Mirrored003
  MapMode = 3
  Placement = pos=(0,0,0) rot=(1,0,0;1.5708rad)
  Support = -> [XY_Plane007]
  X2max = 6.5
  X2min = -6.5
  Xmax = 6.5
  Xmin = -6.5
  Ymax = 11.3
  Ymin = 0
  Z2max = 3.5
  Z2min = -3.5
  Zmax = 3.5
  Zmin = -3.5
FEATURE [PartDesign::AdditiveWedge] Wedge008  label="HoldWedge1"
  AttacherType = Attacher::AttachEngine3D
  BaseFeature = -> Wedge007
  MapMode = 3
  Placement = pos=(0,0,0) rot=(1,0,0;1.5708rad)
  Support = -> [XY_Plane007]
  X2max = 3
  X2min = -3
  Xmax = 3
  Xmin = -3
  Ymax = 9
  Ymin = 6.9
  Z2max = 7
  Z2min = 6
  Zmax = 7
  Zmin = 6.5
FEATURE [PartDesign::Mirrored] Mirrored002
  BaseFeature = -> Wedge008
  MirrorPlane = -> XZ_Plane007
  Originals = -> [Wedge008]
  Placement = pos=(0,0,0) rot=(1,0,0;1.5708rad)
FEATURE [PartDesign::Body] Body004  label="EndHolder001"
  Group = -> [Wedge,Wedge001,Wedge002,Cylinder,Wedge004,Wedge005,Wedge006,Mirrored003,Wedge007,Wedge008,Mirrored002]
  Origin = -> Origin007
  Tip = -> Mirrored002
FEATURE [App::Part] Part002  label="EndHolder"
  Group = -> [Body004]
  Origin = -> Origin006
  Placement = pos=(-240,0,-5.37e-14) rot=(0.57735,-0.57735,-0.57735;2.0944rad)
  expr: .Placement.Base.x = -<<Params>>.SeptumTotalLength / 2 + 10 mm
FEATURE [Part::Mirroring] Mirror  label="EndHolder (mirrored)"
  Base = (0,0,0)
  Normal = (1,0,0)
  Source = -> Part002
note: 1 file-system path scrubbed to <path> (originals preserved in the JSON sidecar)
